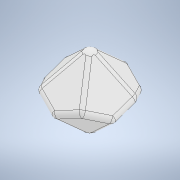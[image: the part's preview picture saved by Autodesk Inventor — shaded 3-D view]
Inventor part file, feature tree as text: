
AUTODESK INVENTOR PART (.ipt)
format: ipt  version: 2021 (Build 250183000, 183)  size: 215,552 bytes
history: native  units: mm
features: sketch x4, extrude x2, pattern_circular x1, fillet x1
ambient origin geometry x8: Origin, YZ Plane, XZ Plane, XY Plane, X Axis, Y Axis, Z Axis, Center Point
bodies: Solid1 (feature_tree)
feature tree (8):
  sketch  "Sketch1"  dims[d0=15.6mm d1=15.6mm]
  extrude  "Extrusion1"  Depth=15.6mm
  extrude  "Extrusion2"  Depth=23.327441mm
  pattern_circular  "Circular Pattern1"  Count=5 Angle=360.0deg
  fillet  "Fillet1"  Radius=1.5mm
  sketch  "Sketch3"  dims[d4=0.0mm]
  sketch  "Sketch4"  dims[d5=0.0mm d6=0.0mm d7=50.0mm d8=360.0deg d10=1.5mm d11=90.0deg d12=21.7mm d13=10.35mm d14=20.7mm d15=21.7mm]
  sketch  "Sketch2"  dims[d2=23.327441mm d3=23.327441mm]
